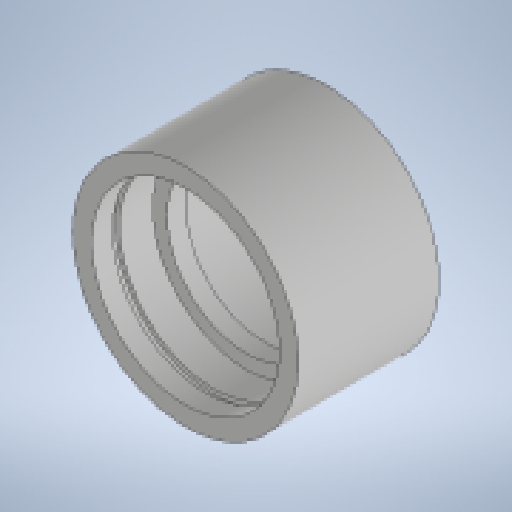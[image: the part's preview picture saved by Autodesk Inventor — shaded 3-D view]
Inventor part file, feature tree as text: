
AUTODESK INVENTOR PART (.ipt)
format: ipt  version: 2025 (Build 290162010, 162A)  size: 256,512 bytes
history: native  units: mm
features: other x1, revolve x1, sketch x1
ambient origin geometry x8: Origin, YZ Plane, XZ Plane, XY Plane, X Axis, Y Axis, Z Axis, Center Point
bodies: Body1 (feature_tree)
feature tree (3):
  other  "Седло для подшипника"
  revolve  "Revolution1"  [1 undecoded]
  sketch  "Sketch6"  dims[d15=4.0mm d16=3.0mm d17=7.0mm d18=1.6mm d19=1.0mm d20=360.0deg d21=48.0mm d22=40.0mm d23=30.0mm]
note: 1 required parameter value undecoded (feature->parameter linkage not recoverable at this tier; creation-order binding heuristic only, values carry confidence <= 0.55)
